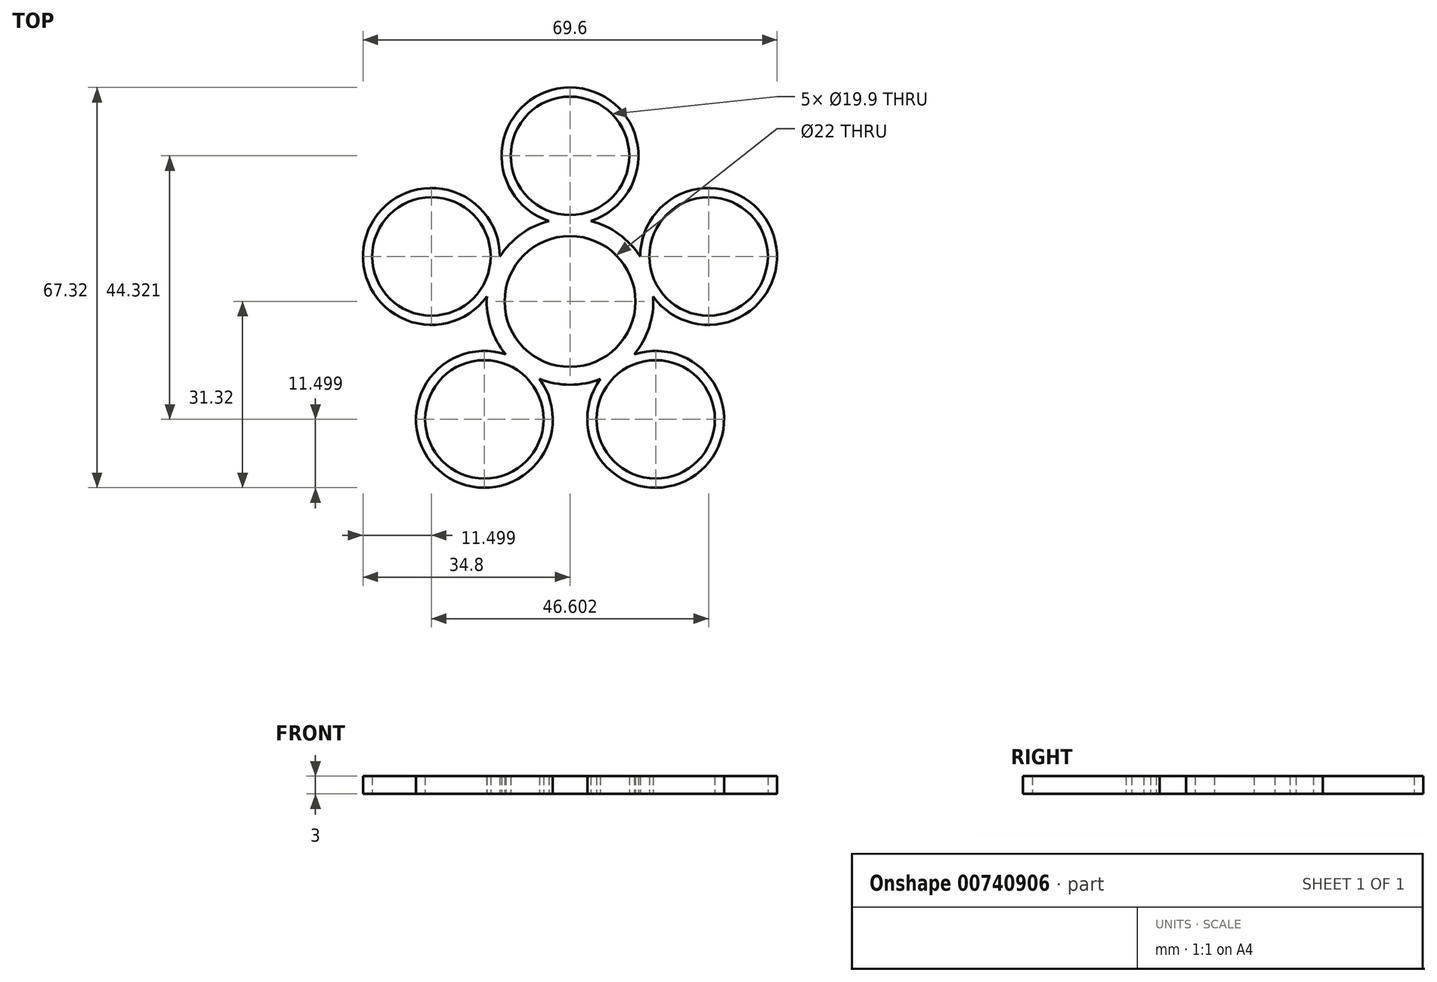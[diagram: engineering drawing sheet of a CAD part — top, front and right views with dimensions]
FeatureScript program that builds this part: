
annotation { "Feature Type Name" : "Feature", "Feature Type Description" : "" }
export const myFeature = defineFeature(function(context is Context, id is Id, definition is map)
    precondition{}
    {
        {
            var Q0;
            Q0=qCreatedBy(makeId("Top.planeOp"),FACE);
            var sketch = newSketch(context, id + "F0", { "sketchPlane" : qUnion([Q0])});
            skArc(sketch, "E0", {"start": v(9.53, 5.5) * mm, "mid": v(0, 11) * mm, "end": v(-9.53, 5.5) * mm});
            skArc(sketch, "E1", {"start": v(-3.52, 13.55) * mm, "mid": v(-8.48, 11.14) * mm, "end": v(-12.12, 7) * mm});
            skCircle(sketch, "E2", {"center": v(0, 24.5) * mm, "radius": 9.95 * mm});
            skArc(sketch, "E3", {"start": v(3.52, 13.55) * mm, "mid": v(0, 36) * mm, "end": v(-3.52, 13.55) * mm});
            skArc(sketch, "E4.trimOffspring", {"start": v(12.12, 7) * mm, "mid": v(8.48, 11.14) * mm, "end": v(3.52, 13.55) * mm});
            skArc(sketch, "E5.1.0", {"start": v(-2.29, 10.76) * mm, "mid": v(-10.46, 3.4) * mm, "end": v(-8.17, -7.36) * mm});
            skArc(sketch, "E5.1.1", {"start": v(-2.91, 13.7) * mm, "mid": v(-7.97, 11.5) * mm, "end": v(-11.8, 7.53) * mm});
            skCircle(sketch, "E5.1.2", {"center": v(-23.3, 7.57) * mm, "radius": 9.95 * mm});
            skArc(sketch, "E5.1.3", {"start": v(-11.8, 7.53) * mm, "mid": v(-34.24, 11.12) * mm, "end": v(-13.97, 0.84) * mm});
            skArc(sketch, "E5.1.4", {"start": v(-13.97, 0.84) * mm, "mid": v(-13.22, -4.62) * mm, "end": v(-10.4, -9.37) * mm});
            skArc(sketch, "E5.2.0", {"start": v(-10.94, 1.15) * mm, "mid": v(-6.47, -8.9) * mm, "end": v(4.47, -10.05) * mm});
            skArc(sketch, "E5.2.1", {"start": v(-13.92, 1.46) * mm, "mid": v(-13.4, -4.03) * mm, "end": v(-10.81, -8.9) * mm});
            skCircle(sketch, "E5.2.2", {"center": v(-14.4, -19.82) * mm, "radius": 9.95 * mm});
            skArc(sketch, "E5.2.3", {"start": v(-10.81, -8.9) * mm, "mid": v(-21.16, -29.12) * mm, "end": v(-5.12, -13.03) * mm});
            skArc(sketch, "E5.2.4", {"start": v(-5.12, -13.03) * mm, "mid": v(0.31, -14) * mm, "end": v(5.7, -12.79) * mm});
            skArc(sketch, "E5.3.0", {"start": v(-4.47, -10.05) * mm, "mid": v(6.47, -8.9) * mm, "end": v(10.94, 1.15) * mm});
            skArc(sketch, "E5.3.1", {"start": v(-5.7, -12.79) * mm, "mid": v(-0.31, -14) * mm, "end": v(5.12, -13.03) * mm});
            skCircle(sketch, "E5.3.2", {"center": v(14.4, -19.82) * mm, "radius": 9.95 * mm});
            skArc(sketch, "E5.3.3", {"start": v(5.12, -13.03) * mm, "mid": v(21.16, -29.12) * mm, "end": v(10.81, -8.9) * mm});
            skArc(sketch, "E5.3.4", {"start": v(10.81, -8.9) * mm, "mid": v(13.4, -4.03) * mm, "end": v(13.92, 1.46) * mm});
            skArc(sketch, "E5.4.0", {"start": v(8.17, -7.36) * mm, "mid": v(10.46, 3.4) * mm, "end": v(2.29, 10.76) * mm});
            skArc(sketch, "E5.4.1", {"start": v(10.4, -9.37) * mm, "mid": v(13.22, -4.62) * mm, "end": v(13.97, 0.84) * mm});
            skCircle(sketch, "E5.4.2", {"center": v(23.3, 7.57) * mm, "radius": 9.95 * mm});
            skArc(sketch, "E5.4.3", {"start": v(13.97, 0.84) * mm, "mid": v(34.24, 11.12) * mm, "end": v(11.8, 7.53) * mm});
            skArc(sketch, "E5.4.4", {"start": v(11.8, 7.53) * mm, "mid": v(7.97, 11.5) * mm, "end": v(2.91, 13.7) * mm});
            skSolve(sketch);
        }
        {
            var Q0;
            Q0 = qSketchRegion(id + "F0", true);
            extrude(context, id + "F1", {"entities" : qUnion([Q0]), "depth" : 3 * mm, "offsetDistance" : 25 * mm});
        }
    });
